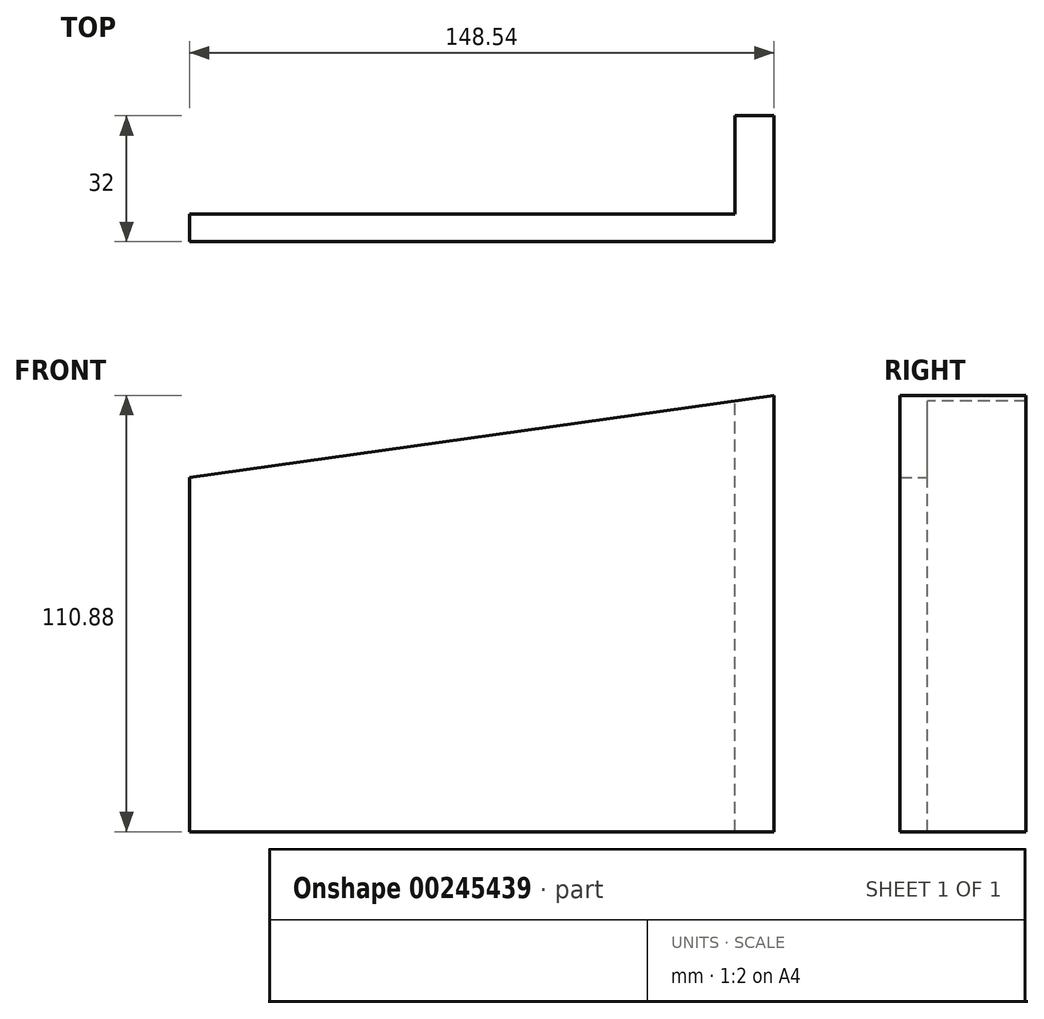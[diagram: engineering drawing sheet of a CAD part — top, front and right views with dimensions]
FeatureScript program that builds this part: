
annotation { "Feature Type Name" : "Feature", "Feature Type Description" : "" }
export const myFeature = defineFeature(function(context is Context, id is Id, definition is map)
    precondition{}
    {
        {
            var Q0;
            Q0=qCreatedBy(makeId("Front.planeOp"),FACE);
            var sketch = newSketch(context, id + "F0", { "sketchPlane" : qUnion([Q0])});
            skLineSegment(sketch, "E0", {"start": v(0, 0) * mm, "end": v(0, 90) * mm});
            skLineSegment(sketch, "E1", {"start": v(0, 90) * mm, "end": v(148.54, 110.88) * mm});
            skLineSegment(sketch, "E2", {"start": v(148.54, 110.88) * mm, "end": v(148.54, 0) * mm});
            skLineSegment(sketch, "E3", {"start": v(148.54, 0) * mm, "end": v(0, 0) * mm});
            skSolve(sketch);
        }
        {
            var Q0;
            Q0=qSketchRegion(id+"F0",true);
            extrude(context, id + "F1", {"entities" : qUnion([Q0]), "depth" : 7 * mm});
        }
        {
            var Q0;
            Q0=makeQuery(id+"F1.opExtrude","CAP_FACE",FACE,{"disambiguationData":[OSD([sQuery(id+"F0.wireOp",EDGE,"E0"),sQuery(id+"F0.wireOp",EDGE,"E1"),sQuery(id+"F0.wireOp",EDGE,"E2"),sQuery(id+"F0.wireOp",EDGE,"E3")])],"isStart":true});
            var sketch = newSketch(context, id + "F2", { "sketchPlane" : qUnion([Q0])});
            skLineSegment(sketch, "E4", {"start": v(-148.54, 110.88) * mm, "end": v(-148.54, 0) * mm});
            skLineSegment(sketch, "E5", {"start": v(-138.54, 109.47) * mm, "end": v(-148.54, 110.88) * mm});
            skLineSegment(sketch, "E6", {"start": v(-148.54, 0) * mm, "end": v(-138.54, 0) * mm});
            skLineSegment(sketch, "E7", {"start": v(-138.54, 0) * mm, "end": v(-138.54, 109.47) * mm});
            skSolve(sketch);
        }
        {
            var Q0;
            Q0=qSketchRegion(id+"F2",true);
            extrude(context, id + "F3", {"entities" : qUnion([Q0]), "operationType" : NewBodyOperationType.ADD, "depth" : 25 * mm});
        }
    });
